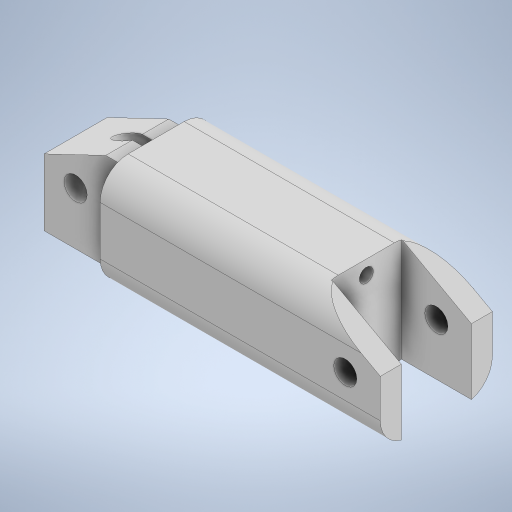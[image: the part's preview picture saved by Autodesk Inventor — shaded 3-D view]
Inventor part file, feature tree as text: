
AUTODESK INVENTOR PART (.ipt)
format: ipt  version: 2024 (Build 280153000, 153)  size: 505,344 bytes
history: native  units: mm
features: sketch x25, extrude x20, chamfer x3, move_body x3, plane x2, split x2, boolean_combine x2, fillet x1
ambient origin geometry x8: Origin, YZ Plane, XZ Plane, XY Plane, X Axis, Y Axis, Z Axis, Center Point
bodies: Solid1 (feature_tree), Solid2 (feature_tree), Solid3 (feature_tree), Solid4 (feature_tree), Solid5 (feature_tree)
feature tree (58):
  extrude  "Extrusion1"  Depth=16.0mm
  sketch  "Sketch2"  dims[d2=15.0mm d3=0.0mm d4=10.0mm]
  extrude  "Extrusion2"  Depth=10.0mm
  chamfer  "Chamfer1"  Distance=21.25mm
  extrude  "Extrusion3"  Depth=10.0mm TaperAngle=0.0deg
  extrude  "Extrusion4"  Depth=11.5mm TaperAngle=0.0deg
  extrude  "Extrusion5"  Depth=1.0mm TaperAngle=0.0deg
  chamfer  "Chamfer2"  Distance=6.0mm Angle=45.0deg
  sketch  "Sketch6"  dims[d14=7.0mm d15=11.5mm d16=0.0mm]
  extrude  "Extrusion6"  Depth=9.0mm
  extrude  "Extrusion7"  Depth=11.5mm TaperAngle=0.0deg
  chamfer  "Chamfer3"  Distance=11.5mm Angle=45.0deg
  sketch  "Sketch9"  dims[d26=3.3mm d27=45.25mm d28=0.0mm d29=11.5mm d30=5.5mm d31=45.0deg]
  extrude  "Extrusion8"  Depth=65.75mm TaperAngle=0.0deg
  extrude  "Extrusion9"  Depth=9.0mm TaperAngle=0.0deg
  extrude  "Extrusion10"  Depth=13.0mm TaperAngle=0.0deg
  sketch  "Sketch13"  dims[d43=24.0mm d44=21.0mm d45=0.0mm]
  extrude  "Extrusion11"  Depth=21.0mm TaperAngle=0.0deg
  extrude  "Extrusion12"  TaperAngle=0.0deg  [1 undecoded]
  extrude  "Extrusion13"  Depth=6.0mm TaperAngle=0.0deg
  plane  "Work Plane1"
  split  "Split1"
  move_body  "Move Body1"
  extrude  "Extrusion14"  Depth=0.5mm TaperAngle=0.0deg
  move_body  "Move Body2"
  fillet  "Fillet1"  Radius=10.0mm
  extrude  "Extrusion15"  Depth=10.0mm TaperAngle=0.0deg
  sketch  "Sketch19"  dims[d71=29.5mm d72=0.0mm d73=13.75mm]
  sketch  "Sketch20"  dims[d74=29.0mm d75=0.0mm d76=-2.0mm d77=0.0mm d78=0.0mm]
  extrude  "Extrusion16"  Depth=1.0mm
  extrude  "Extrusion18"  Depth=13.75mm
  extrude  "Extrusion19"  TaperAngle=0.0deg  [1 undecoded]
  sketch  "Sketch23"
  sketch  "Sketch24"
  extrude  "Extrusion20"  [1 undecoded]
  plane  "Work Plane2"
  boolean_combine  "Combine1"
  split  "Split2"
  extrude  "Extrusion21"  [1 undecoded]
  move_body  "Move Body3"
  boolean_combine  "Combine2"
  sketch  "Sketch1"  dims[d0=36.0mm d1=16.0mm]
  sketch  "Sketch3"  dims[d5=10.0mm]
  sketch  "Sketch4"  dims[d6=3.3mm d7=21.25mm d8=0.0mm]
  sketch  "Sketch5"  dims[d9=10.0mm d10=5.5mm d11=45.0deg d12=10.0mm d13=0.0mm]
  sketch  "Sketch7"  dims[d17=3.3mm d18=1.0mm d19=0.0mm d20=6.0mm d21=11.5mm d22=45.0deg]
  sketch  "Sketch8"  dims[d23=15.0mm d24=0.0mm d25=9.0mm]
  sketch  "Sketch10"  dims[d32=2.0mm d33=65.75mm d34=0.0mm]
  sketch  "Sketch11"  dims[d35=0.5mm d36=0.0mm d37=9.0mm d38=0.0mm]
  sketch  "Sketch12"  dims[d39=0.5mm d40=0.0mm d41=13.0mm d42=0.0mm]
  sketch  "Sketch14"  dims[d46=12.25mm d47=-12.0mm d48=0.0mm d49=0.0mm]
  sketch  "Sketch15"  dims[d50=30.0mm d51=0.0mm d52=6.0mm d53=0.0mm d54=0.0mm d55=4.0mm]
  sketch  "Sketch16"  dims[d56=0.5mm d57=0.0mm d58=0.5mm d59=0.0mm d64=10.0mm d65=0.0mm]
  sketch  "Sketch17"  dims[d66=3.0mm d67=10.0mm d68=0.0mm]
  sketch  "Sketch18"  dims[d69=1.0mm d70=31.0mm]
  sketch  "Sketch22"
  sketch  "Sketch25"
  sketch  "Sketch26"
note: 4 required parameter values undecoded (feature->parameter linkage not recoverable at this tier; creation-order binding heuristic only, values carry confidence <= 0.55)
